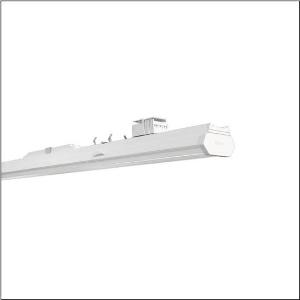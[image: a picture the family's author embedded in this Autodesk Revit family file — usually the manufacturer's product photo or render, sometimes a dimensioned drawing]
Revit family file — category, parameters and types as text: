
# Revit family: licross_r__21_protected_ho_52td12dn4e5m3s_02cf
name_source: partatom
category: Lighting Fixtures
units: mm (PartAtom-declared; Revit-internal decimal feet)

## family parameters
Cut with Voids When Loaded = No
Host = Face
Light Source = No
Part Type = Normal
Room Calculation Point = No
Round Connector Dimension = Use Diameter
Shared = No

## types (1)
- --- (1 x LED, 910 lm, 7.6 W, 4000K)
    Apparent Load = 8 VA
    CIE Flux Codes = 70 91 97 98 100
    Color Rendering = 80
    Color Temperature = 4000K
    Default Elevation = 1800 mm
    Description = Licross® 21 Protected HO, luminaire insert, of sheet steel, galvanised, coil coated, white, length: 1.500mm, width: 90mm, height: 103mm, LED rated luminous flux: 14.690lm, light colour: 840, control gear: DALI 2, with plug, 6-pole, with phase selection, for trunking rail, 14-core, mains connection: 220..240V, AC, 50/60Hz, rated input power: 89W, for trunking rail, 14-core, halogen-free wiring, for emergency light function, converter,control gear: single battery element, battery: LiFeP04, 9Ah, primary light control with lens, of plastic, primary optical cover: cover, of PMMA, light emission: direct distribution, primary light characteristic: symmetric, protection rating (complete): IP54, insulation class (complete): insulation class I (protective earthing), certification: CE, UKCA, protection symbol: D if used in an environment with non-conductive dust loads with corresponding accessories, impact resistance: IK06, permissible ambient temperature for indoor applications: +5..+30°C, standard: EN 60598-2-22, LABS conformity tested according to VDMA 24364:2018-05, reducing of maximum allowable ambient temperature of 5°C with ceiling mounting, corresponds to IFS (International Featured Standards) requirements for safety and quality in the food industry, packaging unit: 1 piece
    Height = 92 mm
    Lamp = 1 x LED
    Lamp Light Flux = 910 lm
    Lamp Power = 7.6 W
    Lamp count = 1
    Length = 1500 mm
    Luminous efficacy = 120 lm/W
    Manufacturer = Siteco
    ModVariant = No
    Model = 52TD12DN4E5M3S
    Mounting Place = Ceiling
    Mounting Type = Pendant
    Number of Poles = 1
    OnlyDefault = Yes
    Power Factor = 1
    Product Name = Licross® 21 Protected HO
    Product group = luminaire insert
    ProductGroupID = 901
    Protection Class = Protection class I
    Protection Degree = IP 54
    RLX_Detail_Level = 1
    RLX_Emergency_Light_Flux = 0 lm
    RLX_Emergency_Type = 0
    RLX_Emergency_Type_DB = No
    RlxData = <blob elided: 24833 chars, md5=20bb3629>
    Socket = socket
    Standby Power = 0 W
    System Light Flux = 910 lm
    System Power = 8 W
    Type Comments = : emergency light operation: 3 h
    Type Image = l_1256148.jpg
    URL = http://relux.com
    VarID = @adj_041315
    Voltage = 0 V
    Weight = 0.00 kg
    Width = 88 mm

## geometry (parser evidence)
native form markers: Blend x4, Sweep x9
no freeform markers — native parametric forms only
